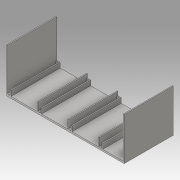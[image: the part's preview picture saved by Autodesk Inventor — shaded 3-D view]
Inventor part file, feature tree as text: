
AUTODESK INVENTOR PART (.ipt)
format: ipt  version: 2016 (Build 200138000, 138)  size: 229,888 bytes
history: native  units: in
note: dims shown in document units (in); Inventor stores cm internally (conversion verified against a paired STEP export)
features: sketch x15, extrude x14, fillet x4
ambient origin geometry x8: Origin, YZ Plane, XZ Plane, XY Plane, X Axis, Y Axis, Z Axis, Center Point
bodies: Solid1 (feature_tree)
feature tree (33):
  extrude  "Extrusion1"  Depth=3.4in TaperAngle=0.0deg
  extrude  "Extrusion2"  Depth=2.95in TaperAngle=0.0deg
  extrude  "Extrusion3"  Depth=0.34in TaperAngle=0.0deg
  extrude  "Extrusion4"  Depth=0.6in TaperAngle=0.0deg
  extrude  "Extrusion5"  Depth=0.34in TaperAngle=0.0deg
  extrude  "Extrusion6"  Depth=0.6in TaperAngle=0.0deg
  extrude  "Extrusion7"  Depth=0.34in TaperAngle=0.0deg
  extrude  "Extrusion8"  Depth=0.6in TaperAngle=0.0deg
  extrude  "Extrusion9"  Depth=0.34in TaperAngle=0.0deg
  sketch  "Sketch14"  dims[d36=0.063in d37=2.83in d38=0.0in]
  extrude  "Extrusion14"  Depth=2.83in TaperAngle=0.0deg
  extrude  "Extrusion15"  Depth=0.063in
  extrude  "Extrusion16"  Depth=0.063in
  extrude  "Extrusion17"  Depth=0.063in
  extrude  "Extrusion18"  Depth=0.09in
  fillet  "Fillet1"  Radius=0.09in
  fillet  "Fillet2"  Radius=0.09in
  fillet  "Fillet3"  Radius=0.09in
  fillet  "Fillet4"  [1 undecoded]
  sketch  "Sketch1"  dims[d0=8.126in d1=3.4in d2=0.0in]
  sketch  "Sketch2"  dims[d3=0.063in d4=2.95in d5=0.0in]
  sketch  "Sketch3"  dims[d6=0.063in d7=0.34in d8=0.0in]
  sketch  "Sketch4"  dims[d9=0.063in d10=0.6in d11=0.0in]
  sketch  "Sketch5"  dims[d12=0.063in d13=0.34in d14=0.0in]
  sketch  "Sketch6"  dims[d15=0.063in d16=0.6in d17=0.0in]
  sketch  "Sketch7"  dims[d18=0.063in d19=0.34in d20=0.0in]
  sketch  "Sketch8"  dims[d21=0.063in d22=0.6in d23=0.0in]
  sketch  "Sketch9"  dims[d24=0.063in d25=0.34in d26=0.0in]
  sketch  "Sketch15"  dims[d39=0.34in d40=0.0in d41=0.063in]
  sketch  "Sketch16"  dims[d42=0.34in d43=0.0in d44=0.063in]
  sketch  "Sketch17"  dims[d45=0.34in d46=0.0in d47=0.063in]
  sketch  "Sketch18"  dims[d48=0.34in d49=0.0in d50=0.09in d51=0.09in d52=0.09in d53=0.09in]
  sketch  "Sketch19"
note: 1 required parameter value undecoded (feature->parameter linkage not recoverable at this tier; creation-order binding heuristic only, values carry confidence <= 0.55)
